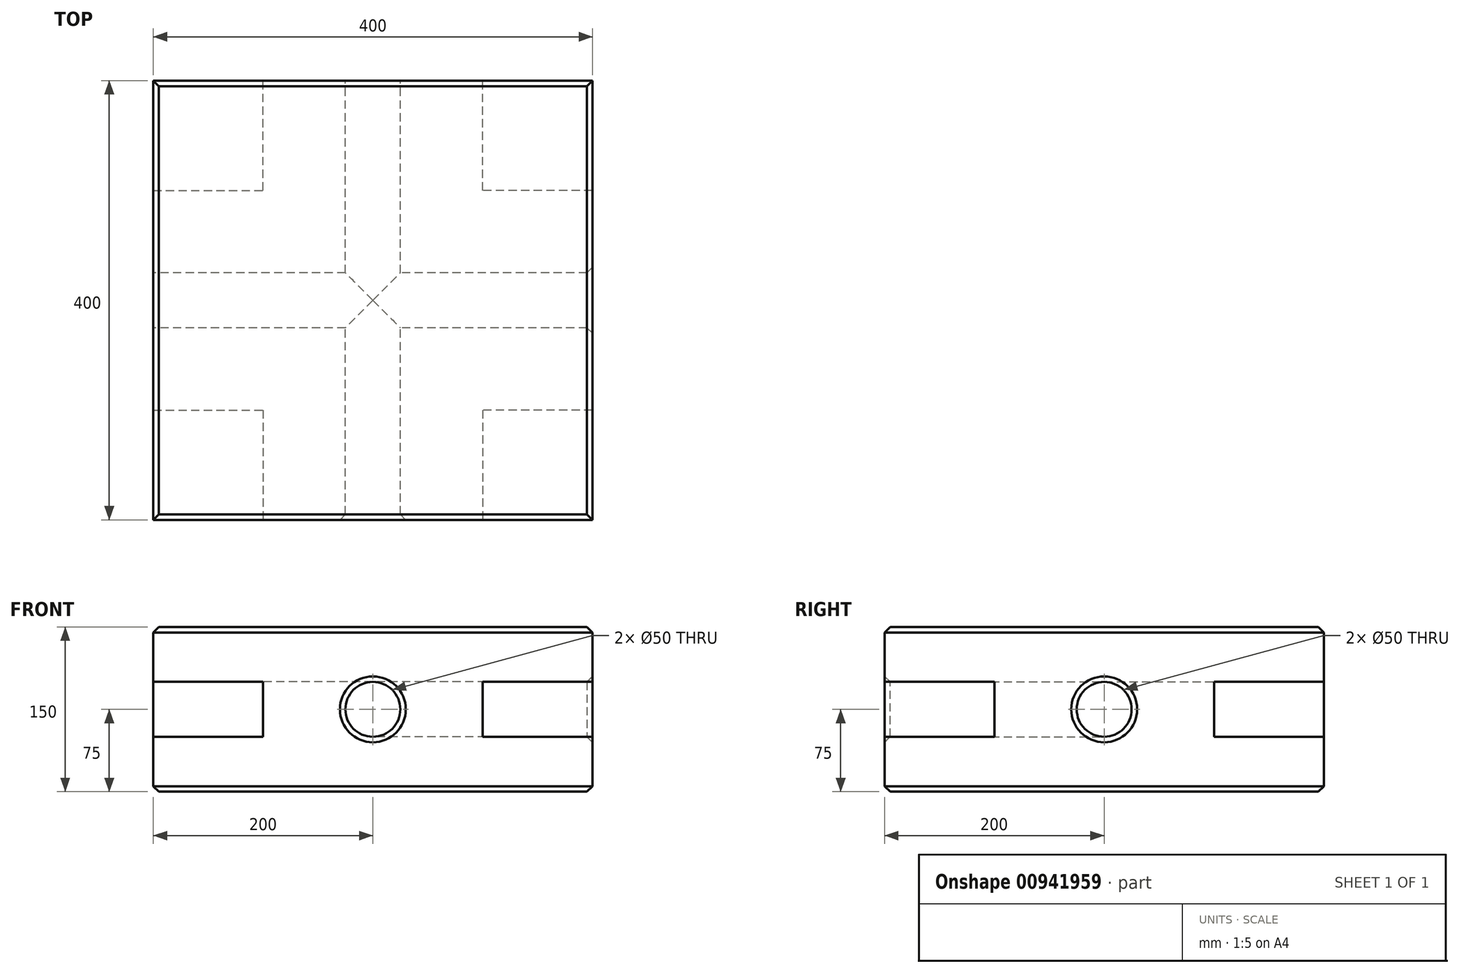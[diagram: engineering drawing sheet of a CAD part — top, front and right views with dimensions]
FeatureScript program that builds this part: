
annotation { "Feature Type Name" : "Feature", "Feature Type Description" : "" }
export const myFeature = defineFeature(function(context is Context, id is Id, definition is map)
    precondition{}
    {
        {
            var Q0;
            Q0=qCreatedBy(makeId("Front.planeOp"),FACE);
            var sketch = newSketch(context, id + "F0", { "sketchPlane" : qUnion([Q0])});
            skLineSegment(sketch, "E0.bottom", {"start": v(200, -75) * mm, "end": v(-200, -75) * mm});
            skLineSegment(sketch, "E0.top", {"start": v(200, 75) * mm, "end": v(-200, 75) * mm});
            skLineSegment(sketch, "E0.left", {"start": v(200, -75) * mm, "end": v(200, 75) * mm});
            skLineSegment(sketch, "E0.right", {"start": v(-200, -75) * mm, "end": v(-200, 75) * mm});
            skPoint(sketch, "E0.middle", {"position": v(0, 0) * mm});
            skSolve(sketch);
        }
        {
            var Q0;
            Q0=makeQuery(id+"F0.imprint","IMPRINT",FACE,{"disambiguationData":[TD([[makeQuery(id+"F0.imprint","IMPRINT",EDGE,{"derivedFrom":sQuery(id+"F0.wireOp",EDGE,"E0.bottom")}),-1.0]])]});
            extrude(context, id + "F1", {"entities" : qUnion([Q0]), "depth" : 400 * mm, "offsetDistance" : 25 * mm});
        }
        {
            var Q0;
            Q0=makeQuery(id+"F1.opExtrude","CAP_FACE",FACE,{"disambiguationData":[OSD([sQuery(id+"F0.wireOp",EDGE,"E0.bottom"),sQuery(id+"F0.wireOp",EDGE,"E0.top"),sQuery(id+"F0.wireOp",EDGE,"E0.left"),sQuery(id+"F0.wireOp",EDGE,"E0.right")])],"isStart":false});
            var sketch = newSketch(context, id + "F2", { "sketchPlane" : qUnion([Q0])});
            skLineSegment(sketch, "E1.0", {"start": v(-200, -75) * mm, "end": v(-200, 75) * mm});
            skLineSegment(sketch, "E2.0", {"start": v(200, -75) * mm, "end": v(200, 75) * mm});
            skLineSegment(sketch, "E3.0", {"start": v(200, 75) * mm, "end": v(-200, 75) * mm});
            skLineSegment(sketch, "E4.0", {"start": v(200, -75) * mm, "end": v(-200, -75) * mm});
            skLineSegment(sketch, "E5.bottom", {"start": v(200, 25) * mm, "end": v(100, 25) * mm});
            skLineSegment(sketch, "E5.top", {"start": v(200, -25) * mm, "end": v(100, -25) * mm});
            skLineSegment(sketch, "E5.left", {"start": v(200, 25) * mm, "end": v(200, -25) * mm});
            skLineSegment(sketch, "E5.right", {"start": v(100, 25) * mm, "end": v(100, -25) * mm});
            skLineSegment(sketch, "E6.bottom", {"start": v(-200, 25) * mm, "end": v(-100, 25) * mm});
            skLineSegment(sketch, "E6.top", {"start": v(-200, -25) * mm, "end": v(-100, -25) * mm});
            skLineSegment(sketch, "E6.left", {"start": v(-200, 25) * mm, "end": v(-200, -25) * mm});
            skLineSegment(sketch, "E6.right", {"start": v(-100, 25) * mm, "end": v(-100, -25) * mm});
            skPoint(sketch, "E7.end.orphan", {"position": v(0, -75) * mm});
            skPoint(sketch, "E7.start.orphan", {"position": v(0, 75) * mm});
            skSolve(sketch);
        }
        {
            var Q0;
            Q0=makeQuery(id+"F2.imprint","IMPRINT",FACE,{"disambiguationData":[TD([[makeQuery(id+"F2.imprint","IMPRINT",EDGE,{"derivedFrom":sQuery(id+"F2.wireOp",EDGE,"E5.bottom")}),1.0]])]});
            var Q1;
            Q1=makeQuery(id+"F2.imprint","IMPRINT",FACE,{"disambiguationData":[TD([[makeQuery(id+"F2.imprint","IMPRINT",EDGE,{"derivedFrom":sQuery(id+"F2.wireOp",EDGE,"E6.bottom")}),-1.0]])]});
            extrude(context, id + "F3", {"entities" : qUnion([Q0, Q1]), "operationType" : NewBodyOperationType.REMOVE, "oppositeDirection" : true, "depth" : 100 * mm, "offsetDistance" : 25 * mm});
        }
        {
            var Q0;
            Q0=makeQuery(id+"F1.opExtrude","CAP_FACE",FACE,{"disambiguationData":[OSD([sQuery(id+"F0.wireOp",EDGE,"E0.bottom"),sQuery(id+"F0.wireOp",EDGE,"E0.top"),sQuery(id+"F0.wireOp",EDGE,"E0.left"),sQuery(id+"F0.wireOp",EDGE,"E0.right")])],"isStart":true});
            var sketch = newSketch(context, id + "F4", { "sketchPlane" : qUnion([Q0])});
            skLineSegment(sketch, "E8.bottom", {"start": v(200, 25) * mm, "end": v(100, 25) * mm});
            skLineSegment(sketch, "E8.top", {"start": v(200, -25) * mm, "end": v(100, -25) * mm});
            skLineSegment(sketch, "E8.left", {"start": v(200, 25) * mm, "end": v(200, -25) * mm});
            skLineSegment(sketch, "E8.right", {"start": v(100, 25) * mm, "end": v(100, -25) * mm});
            skLineSegment(sketch, "E9.bottom", {"start": v(-200, 25) * mm, "end": v(-100, 25) * mm});
            skLineSegment(sketch, "E9.top", {"start": v(-200, -25) * mm, "end": v(-100, -25) * mm});
            skLineSegment(sketch, "E9.left", {"start": v(-200, 25) * mm, "end": v(-200, -25) * mm});
            skLineSegment(sketch, "E9.right", {"start": v(-100, 25) * mm, "end": v(-100, -25) * mm});
            skSolve(sketch);
        }
        {
            var Q0;
            Q0=makeQuery(id+"F4.imprint","IMPRINT",FACE,{"disambiguationData":[TD([[makeQuery(id+"F4.imprint","IMPRINT",EDGE,{"derivedFrom":sQuery(id+"F4.wireOp",EDGE,"E8.bottom")}),1.0]])]});
            var Q1;
            Q1=makeQuery(id+"F4.imprint","IMPRINT",FACE,{"disambiguationData":[TD([[makeQuery(id+"F4.imprint","IMPRINT",EDGE,{"derivedFrom":sQuery(id+"F4.wireOp",EDGE,"E9.bottom")}),-1.0]])]});
            extrude(context, id + "F5", {"entities" : qUnion([Q0, Q1]), "operationType" : NewBodyOperationType.REMOVE, "oppositeDirection" : true, "depth" : 100 * mm, "offsetDistance" : 25 * mm});
        }
        {
            var Q0;
            Q0=makeQuery(id+"F1.opExtrude","CAP_FACE",FACE,{"disambiguationData":[OSD([sQuery(id+"F0.wireOp",EDGE,"E0.bottom"),sQuery(id+"F0.wireOp",EDGE,"E0.top"),sQuery(id+"F0.wireOp",EDGE,"E0.left"),sQuery(id+"F0.wireOp",EDGE,"E0.right")])],"isStart":true});
            var sketch = newSketch(context, id + "F6", { "sketchPlane" : qUnion([Q0])});
            skCircle(sketch, "E10", {"center": v(0, 0) * mm, "radius": 25 * mm});
            skSolve(sketch);
        }
        {
            var Q0;
            Q0=makeQuery(id+"F6.imprint","IMPRINT",FACE,{"disambiguationData":[TD([[makeQuery(id+"F6.imprint","IMPRINT",EDGE,{"derivedFrom":sQuery(id+"F6.wireOp",EDGE,"E10")}),1.0]])]});
            extrude(context, id + "F7", {"entities" : qUnion([Q0]), "operationType" : NewBodyOperationType.REMOVE, "endBound" : BoundingType.THROUGH_ALL, "oppositeDirection" : true, "depth" : 25 * mm, "offsetDistance" : 25 * mm});
        }
        {
            var Q0;
            Q0=makeQuery(id+"F1.opExtrude","SWEPT_FACE",FACE,{"disambiguationData":[OSD([sQuery(id+"F0.wireOp",EDGE,"E0.right")])]});
            var sketch = newSketch(context, id + "F8", { "sketchPlane" : qUnion([Q0])});
            skCircle(sketch, "E11", {"center": v(200, 0) * mm, "radius": 25 * mm});
            skPoint(sketch, "E11.centerSnap0", {"position": v(200, 75) * mm});
            skSolve(sketch);
        }
        {
            var Q0;
            Q0=makeQuery(id+"F8.imprint","IMPRINT",FACE,{"disambiguationData":[TD([[makeQuery(id+"F8.imprint","IMPRINT",EDGE,{"derivedFrom":sQuery(id+"F8.wireOp",EDGE,"E11")}),1.0]])]});
            extrude(context, id + "F9", {"entities" : qUnion([Q0]), "operationType" : NewBodyOperationType.REMOVE, "endBound" : BoundingType.THROUGH_ALL, "oppositeDirection" : true, "depth" : 25 * mm, "offsetDistance" : 25 * mm});
        }
        {
            var Q0;
            Q0=makeQuery(id+"F1.opExtrude","SWEPT_EDGE",EDGE,{"disambiguationData":[OSD([sQuery(id+"F0.wireOp",EDGE,"E0.top"),sQuery(id+"F0.wireOp",EDGE,"E0.right")])]});
            var Q1;
            Q1=makeQuery(id+"F1.opExtrude","SWEPT_EDGE",EDGE,{"disambiguationData":[OSD([sQuery(id+"F0.wireOp",EDGE,"E0.bottom"),sQuery(id+"F0.wireOp",EDGE,"E0.right")])]});
            var Q2;
            Q2=makeQuery(id+"F1.opExtrude","CAP_EDGE",EDGE,{"disambiguationData":[OSD([sQuery(id+"F0.wireOp",EDGE,"E0.top")])],"isStart":true});
            var Q3;
            Q3=makeQuery(id+"F1.opExtrude","CAP_EDGE",EDGE,{"disambiguationData":[OSD([sQuery(id+"F0.wireOp",EDGE,"E0.bottom")])],"isStart":true});
            var Q4;
            Q4=makeQuery(id+"F9.boolean.opBoolean","COPY",EDGE,{"derivedFrom":makeQuery(id+"F9.opExtrude","CAP_EDGE",EDGE,{"disambiguationData":[OSD([sQuery(id+"F8.wireOp",EDGE,"E11")])],"isStart":true})});
            var Q5;
            Q5=makeQuery(id+"F7.boolean.opBoolean","COPY",EDGE,{"derivedFrom":makeQuery(id+"F7.opExtrude","CAP_EDGE",EDGE,{"disambiguationData":[OSD([sQuery(id+"F6.wireOp",EDGE,"E10")])],"isStart":true})});
            var Q6;
            Q6=makeQuery(id+"F1.opExtrude","SWEPT_EDGE",EDGE,{"disambiguationData":[OSD([sQuery(id+"F0.wireOp",EDGE,"E0.bottom"),sQuery(id+"F0.wireOp",EDGE,"E0.left")])]});
            var Q7;
            Q7=makeQuery(id+"F1.opExtrude","SWEPT_EDGE",EDGE,{"disambiguationData":[OSD([sQuery(id+"F0.wireOp",EDGE,"E0.top"),sQuery(id+"F0.wireOp",EDGE,"E0.left")])]});
            var Q8;
            Q8=makeQuery(id+"F9.boolean.opBoolean","INTERSECT",EDGE,{"derivedFrom":[makeQuery(id+"F1.opExtrude","SWEPT_FACE",FACE,{"disambiguationData":[OSD([sQuery(id+"F0.wireOp",EDGE,"E0.left")])]}),makeQuery(id+"F9.opExtrude","SWEPT_FACE",FACE,{"disambiguationData":[OSD([sQuery(id+"F8.wireOp",EDGE,"E11")])]})]});
            var Q9;
            Q9=makeQuery(id+"F1.opExtrude","CAP_EDGE",EDGE,{"disambiguationData":[OSD([sQuery(id+"F0.wireOp",EDGE,"E0.bottom")])],"isStart":false});
            var Q10;
            Q10=makeQuery(id+"F1.opExtrude","CAP_EDGE",EDGE,{"disambiguationData":[OSD([sQuery(id+"F0.wireOp",EDGE,"E0.top")])],"isStart":false});
            var Q11;
            Q11=makeQuery(id+"F7.boolean.opBoolean","INTERSECT",EDGE,{"derivedFrom":[makeQuery(id+"F1.opExtrude","CAP_FACE",FACE,{"disambiguationData":[OSD([sQuery(id+"F0.wireOp",EDGE,"E0.bottom"),sQuery(id+"F0.wireOp",EDGE,"E0.top"),sQuery(id+"F0.wireOp",EDGE,"E0.left"),sQuery(id+"F0.wireOp",EDGE,"E0.right")])],"isStart":false}),makeQuery(id+"F7.opExtrude","SWEPT_FACE",FACE,{"disambiguationData":[OSD([sQuery(id+"F6.wireOp",EDGE,"E10")])]})]});
            chamfer(context, id + "F10", {"entities" : qUnion([Q0, Q1, Q2, Q3, Q4, Q5, Q6, Q7, Q8, Q9, Q10, Q11]), "width" : 5 * mm, "tangentPropagation" : true});
        }
    });
